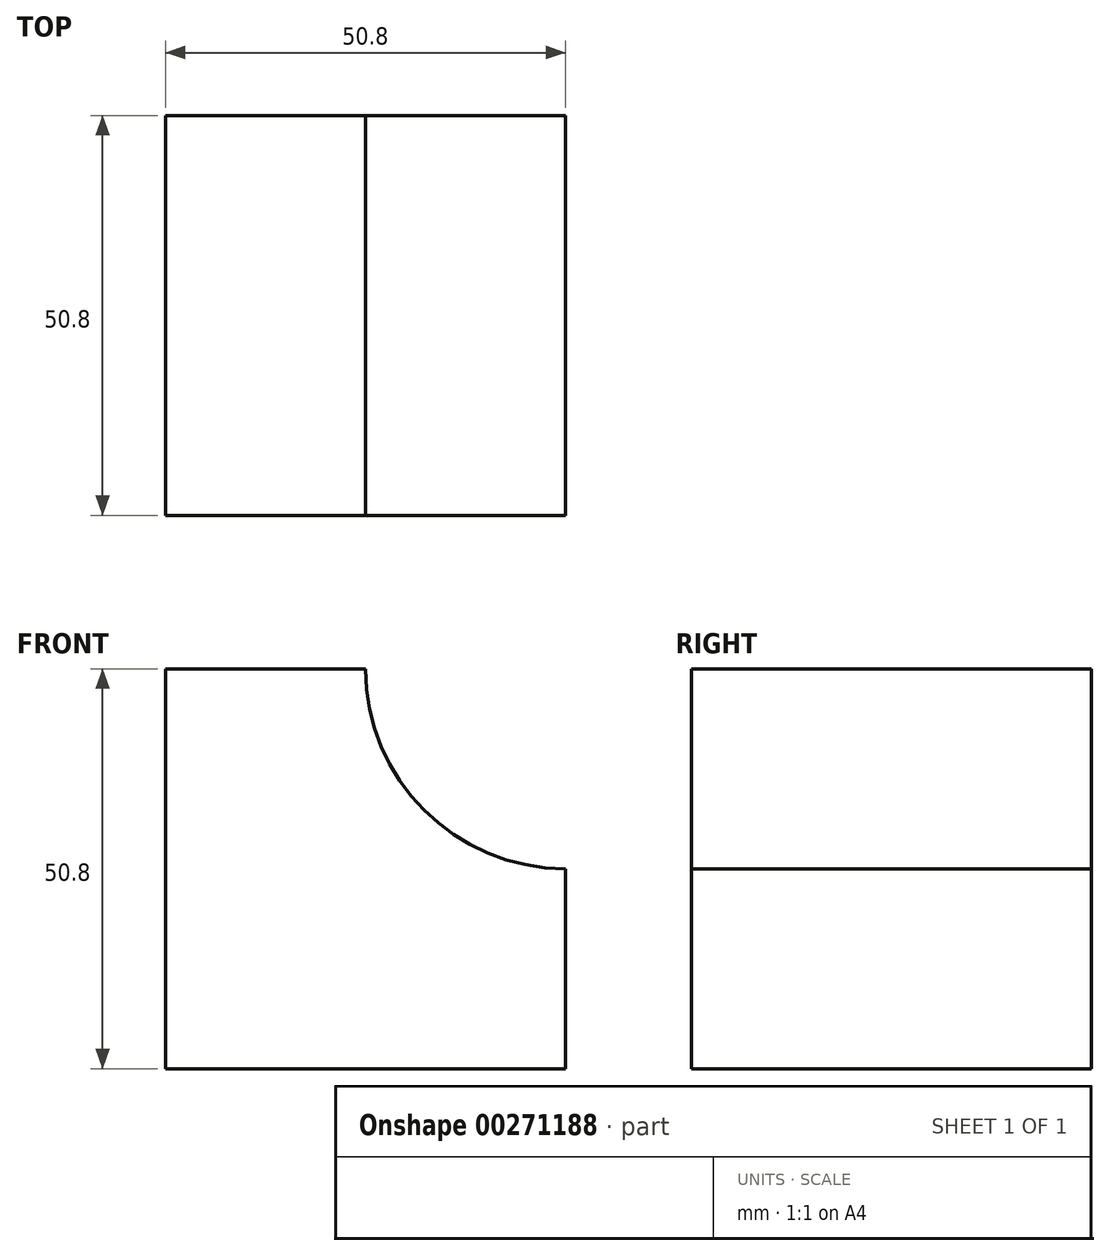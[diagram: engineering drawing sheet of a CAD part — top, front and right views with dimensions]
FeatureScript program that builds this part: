
annotation { "Feature Type Name" : "Feature", "Feature Type Description" : "" }
export const myFeature = defineFeature(function(context is Context, id is Id, definition is map)
    precondition{}
    {
        {
            var Q0;
            Q0=qCreatedBy(makeId("Front.planeOp"),FACE);
            var sketch = newSketch(context, id + "F0", { "sketchPlane" : qUnion([Q0])});
            skLineSegment(sketch, "E0", {"start": v(0, 0) * mm, "end": v(-50.8, 0) * mm});
            skLineSegment(sketch, "E1", {"start": v(-50.8, 0) * mm, "end": v(-50.8, 50.8) * mm});
            skLineSegment(sketch, "E2", {"start": v(-50.8, 50.8) * mm, "end": v(-25.4, 50.8) * mm});
            skLineSegment(sketch, "E3", {"start": v(0, 25.4) * mm, "end": v(0, 0) * mm});
            skArc(sketch, "E4", {"start": v(-25.4, 50.8) * mm, "mid": v(-17.96, 32.84) * mm, "end": v(0, 25.4) * mm});
            skSolve(sketch);
        }
        {
            var Q0;
            Q0 = qSketchRegion(id + "F0", true);
            extrude(context, id + "F1", {"entities" : qUnion([Q0]), "depth" : 50.8 * mm});
        }
    });
